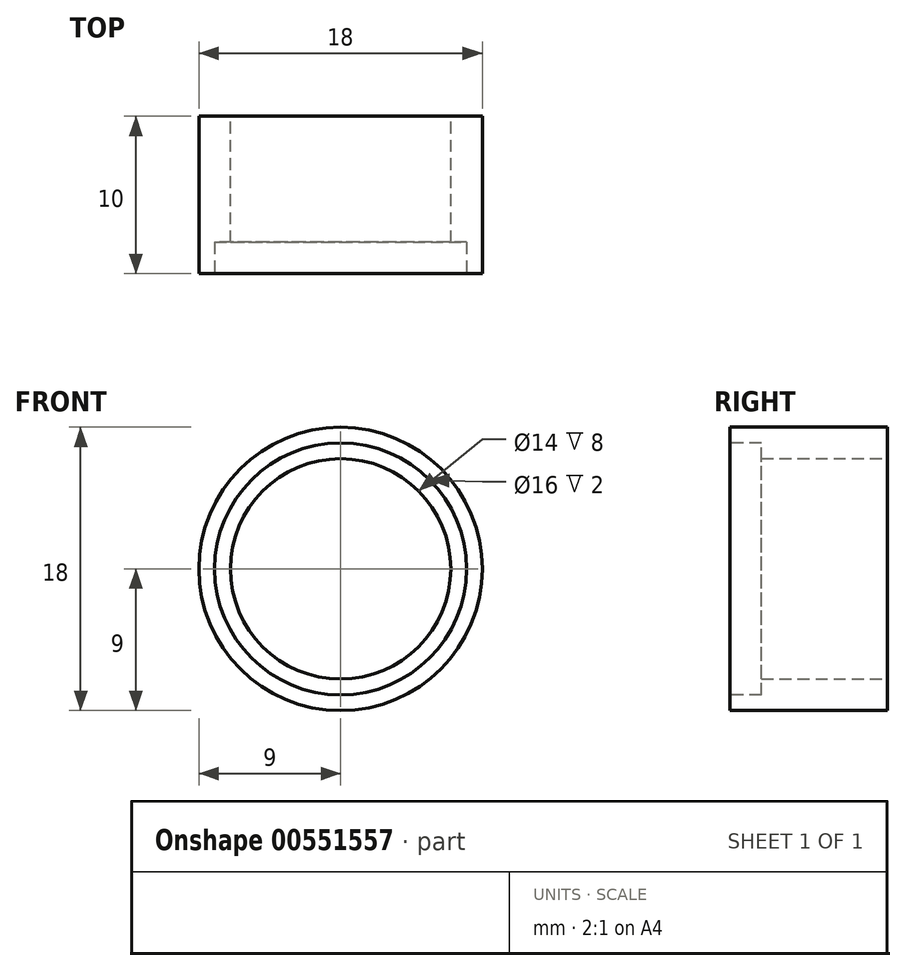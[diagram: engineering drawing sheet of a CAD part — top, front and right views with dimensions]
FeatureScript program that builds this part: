
annotation { "Feature Type Name" : "Feature", "Feature Type Description" : "" }
export const myFeature = defineFeature(function(context is Context, id is Id, definition is map)
    precondition{}
    {
        {
            var Q0;
            Q0=qCreatedBy(makeId("Front.planeOp"),FACE);
            var sketch = newSketch(context, id + "F0", { "sketchPlane" : qUnion([Q0])});
            skCircle(sketch, "E0", {"center": v(0, 0) * mm, "radius": 9 * mm});
            skCircle(sketch, "E1", {"center": v(0, 0) * mm, "radius": 7 * mm});
            skSolve(sketch);
        }
        {
            var Q0;
            Q0=qSketchRegion(id+"F0",true);
            extrude(context, id + "F1", {"entities" : qUnion([Q0]), "depth" : 10 * mm, "offsetDistance" : 25 * mm});
        }
        {
            var Q0;
            Q0=qCreatedBy(makeId("Front.planeOp"),FACE);
            cPlane(context, id + "F2", {"entities" : qUnion([Q0]), "cplaneType" : CPlaneType.OFFSET, "offset" : 10 * mm, "width" : 150 * mm, "height" : 150 * mm});
        }
        {
            var Q0;
            Q0=qCreatedBy(id+"F2.planeOp",FACE);
            var sketch = newSketch(context, id + "F3", { "sketchPlane" : qUnion([Q0])});
            skCircle(sketch, "E2", {"center": v(0, 0) * mm, "radius": 8 * mm});
            skSolve(sketch);
        }
        {
            var Q0;
            Q0=qSketchRegion(id+"F3",true);
            extrude(context, id + "F4", {"entities" : qUnion([Q0]), "operationType" : NewBodyOperationType.REMOVE, "oppositeDirection" : true, "depth" : 2 * mm, "offsetDistance" : 25 * mm});
        }
    });
